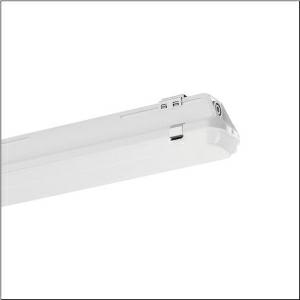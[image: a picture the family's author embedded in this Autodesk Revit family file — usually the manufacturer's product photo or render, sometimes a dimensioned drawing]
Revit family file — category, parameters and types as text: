
# Revit family: monsun_r__21_51fb10mp680c_b42b
name_source: partatom
category: Lighting Fixtures
units: mm (PartAtom-declared; Revit-internal decimal feet)

## family parameters
Cut with Voids When Loaded = No
Host = Face
Light Source = No
Part Type = Normal
Room Calculation Point = No
Round Connector Dimension = Use Diameter
Shared = No

## types (1)
- --- (1 x LED, 8200 lm, 46.9 W, 6500K)
    Apparent Load = 47 VA
    CIE Flux Codes = 47 77 93 94 100
    Color Rendering = 80
    Color Temperature = 6500K
    Default Elevation = 1800 mm
    Description = Monsun® 21, damp-proof luminaire, chain hanger, primary optical cover: enclosure, of PMMA, light emission: direct distribution, primary light characteristic: symmetric, installation type: suspended mounting, surface-mounted, horizontal mounting, vertical mounting, LED, rated luminous flux: 8.200lm, luminous efficacy: 175lm/W, light colour: 865, colour temperature: 6500K, control gear: ON/OFF Multilumen, with terminal, 3-pole, max. 2.5mm², mains connection: 220..240V, AC, 50/60Hz, rated input power: 47W, housing, of glass-fibre reinforced polyester, uncoated, bright grey, incl. chain hanger, length: 1.590mm, width: 90mm, height: 88mm, clip for enclosure, of stainless steel (V2A), ceiling mounting element, of stainless steel (V2A), chain hanger, of stainless steel (V2A), protection rating (complete): IP66, insulation class (complete): insulation class I (protective earthing), certification: CE, ENEC, VDE, UKCA, protection symbol: D, impact resistance: IK04, permissible operating ambient temperature: -25..+35°C, standard: EN 50419, EN 60598-2-1, corresponds to IFS (International Featured Standards) requirements for safety and quality in the food industry, for indoor or canopied outdoor use, no direct snow, no direct sun, no direct rain, LABS conformity tested according to VDMA 24364:2018-05, contact your sales advisor before using the luminaires in applications with unclear chemical exposure, large temperature fluctuations or condensation-forming humidity, packaging unit: 1 piece
    Height = 89 mm
    Lamp = 1 x LED
    Lamp Light Flux = 8200 lm
    Lamp Power = 46.9 W
    Lamp count = 1
    Length = 1590 mm
    Luminous efficacy = 175 lm/W
    Manufacturer = Siteco
    ModVariant = No
    Model = 51FB10MP680C
    Mounting Place = Ceiling
    Mounting Type = Surface mounted
    Number of Poles = 1
    OnlyDefault = Yes
    Power Factor = 1
    Product Name = Monsun® 21
    Product group = damp-proof luminaire
    ProductGroupID = 301
    Protection Class = Protection class I
    Protection Degree = IP 66
    RLX_Detail_Level = 1
    RLX_Emergency_Light_Flux = 0 lm
    RLX_Emergency_Type = 0
    RLX_Emergency_Type_DB = No
    RlxData = <blob elided: 90005 chars, md5=fc19c061>
    Socket = socket
    Standby Power = 0 W
    System Light Flux = 8200 lm
    System Power = 47 W
    Type Comments = factory setting: luminous flux: 100 % | (A | C | E) | 109 mA
    Type Image = l_1319656.jpg
    URL = http://relux.com
    VarID = @adj_051779
    Voltage = 0 V
    Weight = 0.00 kg
    Width = 90 mm

## geometry (parser evidence)
native form markers: Blend x4, Sweep x12
no freeform markers — native parametric forms only
